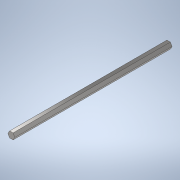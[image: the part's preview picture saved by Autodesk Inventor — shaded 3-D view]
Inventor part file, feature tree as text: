
AUTODESK INVENTOR PART (.ipt)
format: ipt  version: 2020 (Build 240168000, 168)  size: 102,912 bytes
history: native  units: in
note: dims shown in document units (in); Inventor stores cm internally (conversion verified against a paired STEP export)
features: extrude x1, sketch x1
ambient origin geometry x8: Origin, YZ Plane, XZ Plane, XY Plane, X Axis, Y Axis, Z Axis, Center Point
bodies: Solid1 (feature_tree)
feature tree (2):
  extrude  "Extrusion1"  Depth=13.0in TaperAngle=0.0deg
  sketch  "Sketch1"  dims[d0=0.5in d1=13.0in d2=0.0in]
